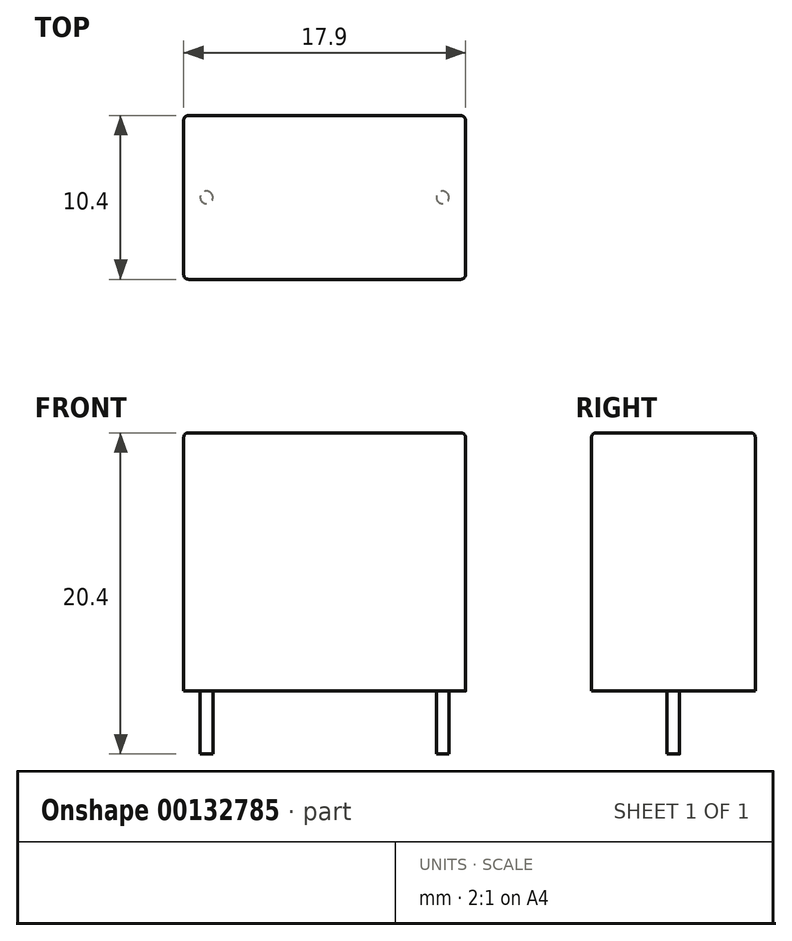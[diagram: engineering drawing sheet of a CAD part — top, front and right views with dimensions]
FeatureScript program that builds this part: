
annotation { "Feature Type Name" : "Feature", "Feature Type Description" : "" }
export const myFeature = defineFeature(function(context is Context, id is Id, definition is map)
    precondition{}
    {
        {
            var Q0;
            Q0=qCreatedBy(makeId("Top.planeOp"),FACE);
            var sketch = newSketch(context, id + "F0", { "sketchPlane" : qUnion([Q0])});
            skLineSegment(sketch, "E0.bottom", {"start": v(-8.95, 5.2) * mm, "end": v(8.95, 5.2) * mm});
            skLineSegment(sketch, "E0.top", {"start": v(-8.95, -5.2) * mm, "end": v(8.95, -5.2) * mm});
            skLineSegment(sketch, "E0.left", {"start": v(-8.95, 5.2) * mm, "end": v(-8.95, -5.2) * mm});
            skLineSegment(sketch, "E0.right", {"start": v(8.95, 5.2) * mm, "end": v(8.95, -5.2) * mm});
            skPoint(sketch, "E0.middle", {"position": v(0, 0) * mm});
            skSolve(sketch);
        }
        {
            var Q0;
            Q0 = qSketchRegion(id + "F0", true);
            extrude(context, id + "F1", {"entities" : qUnion([Q0]), "depth" : 16.4 * mm, "offsetDistance" : 25 * mm});
        }
        {
            var Q0;
            Q0=makeQuery(id+"F1.opExtrude","CAP_FACE",FACE,{"disambiguationData":[OSD([sQuery(id+"F0.wireOp",EDGE,"E0.bottom"),sQuery(id+"F0.wireOp",EDGE,"E0.top"),sQuery(id+"F0.wireOp",EDGE,"E0.left"),sQuery(id+"F0.wireOp",EDGE,"E0.right")])],"isStart":false});
            var Q1;
            Q1=makeQuery(id+"F1.opExtrude","SWEPT_EDGE",EDGE,{"disambiguationData":[OSD([sQuery(id+"F0.wireOp",EDGE,"E0.top"),sQuery(id+"F0.wireOp",EDGE,"E0.right")])]});
            var Q2;
            Q2=makeQuery(id+"F1.opExtrude","SWEPT_EDGE",EDGE,{"disambiguationData":[OSD([sQuery(id+"F0.wireOp",EDGE,"E0.bottom"),sQuery(id+"F0.wireOp",EDGE,"E0.right")])]});
            var Q3;
            Q3=makeQuery(id+"F1.opExtrude","SWEPT_EDGE",EDGE,{"disambiguationData":[OSD([sQuery(id+"F0.wireOp",EDGE,"E0.bottom"),sQuery(id+"F0.wireOp",EDGE,"E0.left")])]});
            var Q4;
            Q4=makeQuery(id+"F1.opExtrude","SWEPT_EDGE",EDGE,{"disambiguationData":[OSD([sQuery(id+"F0.wireOp",EDGE,"E0.top"),sQuery(id+"F0.wireOp",EDGE,"E0.left")])]});
            fillet(context, id + "F2", {"entities" : qUnion([Q0, Q1, Q2, Q3, Q4]), "radius" : 0.3 * mm, "tangentPropagation" : true, "allowEdgeOverflow" : false});
        }
        {
            var Q0;
            Q0=qCreatedBy(makeId("Top.planeOp"),FACE);
            var sketch = newSketch(context, id + "F3", { "sketchPlane" : qUnion([Q0])});
            skCircle(sketch, "E1", {"center": v(-7.5, 0) * mm, "radius": 0.4 * mm});
            skCircle(sketch, "E2.MirrorC", {"center": v(7.5, 0) * mm, "radius": 0.4 * mm});
            skSolve(sketch);
        }
        {
            var Q0;
            Q0 = qSketchRegion(id + "F3", true);
            extrude(context, id + "F4", {"entities" : qUnion([Q0]), "oppositeDirection" : true, "depth" : 4 * mm, "offsetDistance" : 25 * mm});
        }
    });
